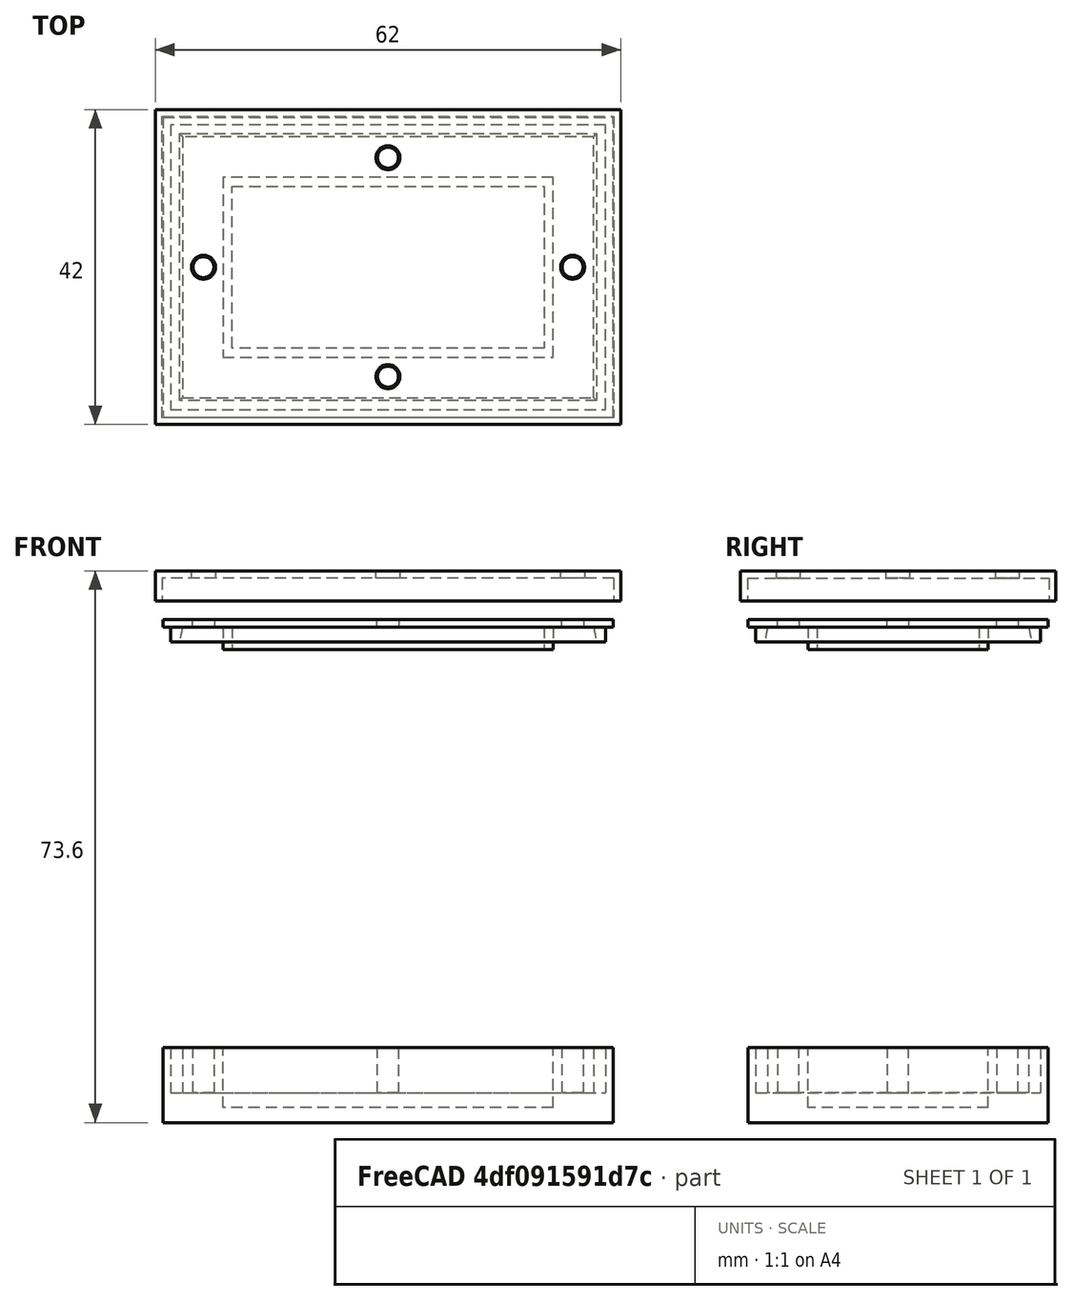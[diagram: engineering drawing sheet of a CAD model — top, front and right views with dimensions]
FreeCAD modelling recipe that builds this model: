
FCSTD DOCUMENT  (FreeCAD 1.0R39109 (Git))
Label: SealTest2
License: All rights reserved
objects: Sketcher::SketchObject×9, PartDesign::Pad×6, PartDesign::SubShapeBinder×4, PartDesign::Body×3, PartDesign::Pocket×1, PartDesign::AdditiveLoft×1
note: 49 computed .brp shape members not serialized (recipe doc carries the construction recipe); baked Part::Feature solids carry a one-line shape summary decoded from their .brp

FEATURE [Sketcher::SketchObject] Sketch  label="BaseSketch"
  ArcFitTolerance = 1e-06
  AttachmentSupport = -> [XY_Plane]
  FullyConstrained = true
  MakeInternals = false
  MapMode = 5
  sketch-geometry (4):
    g0: LineSegment StartX=-30 StartY=20 StartZ=0 EndX=-30 EndY=-20 EndZ=0
    g1: LineSegment StartX=-30 StartY=-20 StartZ=0 EndX=30 EndY=-20 EndZ=0
    g2: LineSegment StartX=30 StartY=-20 StartZ=0 EndX=30 EndY=20 EndZ=0
    g3: LineSegment StartX=30 StartY=20 StartZ=0 EndX=-30 EndY=20 EndZ=0
  constraints (11):
    c: Coincident(g0,g1)
    c: Coincident(g1,g2)
    c: Coincident(g2,g3)
    c: Coincident(g3,g0)
    c: Vertical(g0)
    c: Vertical(g2)
    c: Horizontal(g1)
    c: Horizontal(g3)
    c: DistanceX(g3,g3) = 60  'length'
    c: DistanceY(g2,g2) = 40  'width'
    c: Symmetric(g0,g2,g-1)
FEATURE [PartDesign::Pad] Pad  label="Base"
  Direction = (0,0,1)
  Length = 2
  Length2 = 10
  Profile = -> Sketch
  ReferenceAxis = -> Sketch [N_Axis]
  Suppressed = false
  Type = 0
FEATURE [Sketcher::SketchObject] Sketch001  label="WallSketch"
  ArcFitTolerance = 1e-06
  AttachmentSupport = -> [XY_Plane]
  FullyConstrained = true
  MakeInternals = false
  MapMode = 5
  expr: Constraints[10] = Sketch.Constraints.length
  expr: Constraints[11] = Sketch.Constraints.width
  sketch-geometry (10):
    g0: LineSegment StartX=30 StartY=-20 StartZ=0 EndX=30 EndY=20 EndZ=0
    g1: LineSegment StartX=30 StartY=20 StartZ=0 EndX=-30 EndY=20 EndZ=0
    g2: LineSegment StartX=-30 StartY=20 StartZ=0 EndX=-30 EndY=-20 EndZ=0
    g3: LineSegment StartX=-30 StartY=-20 StartZ=0 EndX=30 EndY=-20 EndZ=0
    g4: GeomPoint [constr] X=0 Y=0 Z=0
    g5: LineSegment StartX=22 StartY=-12 StartZ=0 EndX=22 EndY=12 EndZ=0
    g6: LineSegment StartX=22 StartY=12 StartZ=0 EndX=-22 EndY=12 EndZ=0
    g7: LineSegment StartX=-22 StartY=12 StartZ=0 EndX=-22 EndY=-12 EndZ=0
    g8: LineSegment StartX=-22 StartY=-12 StartZ=0 EndX=22 EndY=-12 EndZ=0
    g9: GeomPoint [constr] X=0 Y=0 Z=0
  constraints (24):
    c: Coincident(g0,g1)
    c: Coincident(g1,g2)
    c: Coincident(g2,g3)
    c: Coincident(g3,g0)
    c: Vertical(g0)
    c: Vertical(g2)
    c: Horizontal(g1)
    c: Horizontal(g3)
    c: Symmetric(g2,g0,g4)
    c: Coincident(g4,g-1)
    c: DistanceX(g1,g1) = 60
    c: DistanceY(g0,g0) = 40
    c: Coincident(g5,g6)
    c: Coincident(g6,g7)
    c: Coincident(g7,g8)
    c: Coincident(g8,g5)
    c: Vertical(g5)
    c: Vertical(g7)
    c: Horizontal(g6)
    c: Horizontal(g8)
    c: Symmetric(g7,g5,g9)
    c: Coincident(g9,g4)
    c: DistanceX(g1,g6) = 8
    c: DistanceY(g6,g1) = 8  'WallThickness'
FEATURE [PartDesign::Pad] Pad001  label="Wall"
  BaseFeature = -> Pad
  Direction = (0,0,1)
  Length = 10
  Length2 = 10
  Profile = -> Sketch001
  ReferenceAxis = -> Sketch001 [N_Axis]
  Suppressed = false
  Type = 0
FEATURE [Sketcher::SketchObject] Sketch002  label="SealGapSketch"
  ArcFitTolerance = 1e-06
  AttachmentSupport = -> [Pad001]
  ExternalGeometry = -> [Pad001]
  FullyConstrained = true
  MakeInternals = false
  MapMode = 5
  Placement = pos=(0,0,10) rot=(0,0,1;0rad)
  expr: Constraints[28] = <<WallSketch>>.Constraints.WallThickness - (.Constraints.SealFromSide + .Constraints.SealWidth)
  expr: Constraints[29] = <<WallSketch>>.Constraints.WallThickness - (.Constraints.SealFromSide + .Constraints.SealWidth)
  expr: Constraints[30] = <<WallSketch>>.Constraints.WallThickness - (.Constraints.SealFromSide + .Constraints.SealWidth)
  expr: Constraints[31] = <<WallSketch>>.Constraints.WallThickness - (.Constraints.SealFromSide + .Constraints.SealWidth)
  sketch-geometry (22):
    g0: LineSegment StartX=-27.4 StartY=17.4 StartZ=0 EndX=-27.4 EndY=-17.4 EndZ=0
    g1: LineSegment StartX=-27.4 StartY=-17.4 StartZ=0 EndX=27.4 EndY=-17.4 EndZ=0
    g2: LineSegment StartX=27.4 StartY=-17.4 StartZ=0 EndX=27.4 EndY=17.4 EndZ=0
    g3: LineSegment StartX=27.4 StartY=17.4 StartZ=0 EndX=-27.4 EndY=17.4 EndZ=0
    g4: GeomPoint [constr] X=0 Y=0 Z=0
    g5: LineSegment StartX=-29 StartY=-19 StartZ=0 EndX=29 EndY=-19 EndZ=0
    g6: LineSegment StartX=29 StartY=-19 StartZ=0 EndX=29 EndY=19 EndZ=0
    g7: LineSegment StartX=29 StartY=19 StartZ=0 EndX=-29 EndY=19 EndZ=0
    g8: LineSegment StartX=-29 StartY=19 StartZ=0 EndX=-29 EndY=-19 EndZ=0
    g9: GeomPoint [constr] X=0 Y=0 Z=0
    g10: Circle CenterX=0 CenterY=14.6 CenterZ=0 NormalX=0 NormalY=0 NormalZ=1 AngleXU=0 Radius=1.4
    g11: Circle CenterX=24.6 CenterY=0 CenterZ=0 NormalX=0 NormalY=0 NormalZ=1 AngleXU=0 Radius=1.4
    g12: Circle CenterX=0 CenterY=-14.6 CenterZ=0 NormalX=0 NormalY=0 NormalZ=1 AngleXU=0 Radius=1.4
    g13: Circle CenterX=-24.6 CenterY=0 CenterZ=0 NormalX=0 NormalY=0 NormalZ=1 AngleXU=0 Radius=1.4
    g14: LineSegment [constr] StartX=-30 StartY=20 StartZ=0 EndX=-30 EndY=19 EndZ=0
    g15: LineSegment [constr] StartX=-30 StartY=19 StartZ=0 EndX=-29 EndY=19 EndZ=0
    g16: LineSegment [constr] StartX=-29 StartY=19 StartZ=0 EndX=-29 EndY=20 EndZ=0
    g17: LineSegment [constr] StartX=-29 StartY=20 StartZ=0 EndX=-30 EndY=20 EndZ=0
    g18: LineSegment [constr] StartX=-29 StartY=19 StartZ=0 EndX=-29 EndY=17.4 EndZ=0
    g19: LineSegment [constr] StartX=-29 StartY=17.4 StartZ=0 EndX=-27.4 EndY=17.4 EndZ=0
    g20: LineSegment [constr] StartX=-27.4 StartY=17.4 StartZ=0 EndX=-27.4 EndY=19 EndZ=0
    g21: LineSegment [constr] StartX=-27.4 StartY=19 StartZ=0 EndX=-29 EndY=19 EndZ=0
  constraints (56):
    c: Coincident(g0,g1)
    c: Coincident(g1,g2)
    c: Coincident(g2,g3)
    c: Coincident(g3,g0)
    c: Vertical(g0)
    c: Vertical(g2)
    c: Horizontal(g1)
    c: Horizontal(g3)
    c: Symmetric(g2,g0,g4)
    c: Coincident(g4,g-1)
    c: Coincident(g5,g6)
    c: Coincident(g6,g7)
    c: Coincident(g7,g8)
    c: Coincident(g8,g5)
    c: Horizontal(g5)
    c: Horizontal(g7)
    c: Vertical(g6)
    c: Vertical(g8)
    c: Symmetric(g7,g5,g9)
    c: Coincident(g9,g4)
    c: PointOnObject(g10,g-2)
    c: PointOnObject(g11,g-1)
    c: PointOnObject(g12,g-2)
    c: PointOnObject(g13,g-1)
    c: Equal(g13,g10)
    c: Equal(g10,g11)
    c: Equal(g11,g12)
    c: Diameter(g10) = 2.8
    c: DistanceY(g10,g-3) = 5.4
    c: DistanceX(g-3,g13) = 5.4
    c: DistanceX(g11,g-3) = 5.4
    c: DistanceY(g-4,g12) = 5.4
    c: Coincident(g14,g15)
    c: Coincident(g15,g16)
    c: Coincident(g16,g17)
    c: Coincident(g17,g14)
    c: Vertical(g14)
    c: Vertical(g16)
    c: Horizontal(g15)
    c: Horizontal(g17)
    c: Coincident(g14,g-3)
    c: Coincident(g15,g7)
    c: Equal(g16,g15)
    c: Coincident(g18,g19)
    c: Coincident(g19,g20)
    c: Coincident(g20,g21)
    c: Coincident(g21,g18)
    c: Vertical(g18)
    c: Vertical(g20)
    c: Horizontal(g19)
    c: Horizontal(g21)
    c: Coincident(g18,g7)
    c: Coincident(g19,g0)
    c: Equal(g20,g19)
    c: DistanceX(g14,g16) = 1  'SealFromSide'
    c: DistanceX(g7,g20) = 1.6  'SealWidth'
FEATURE [PartDesign::Pocket] Pocket  label="SealGap"
  BaseFeature = -> Pad001
  Direction = (0,0,-1)
  Length = 6
  Length2 = 5
  Profile = -> Sketch002
  ReferenceAxis = -> Sketch002 [N_Axis]
  Suppressed = false
  Type = 0
FEATURE [PartDesign::Body] Body  label="Base001"
  AllowCompound = false
  Group = -> [Sketch,Pad,Sketch001,Pad001,Sketch002,Pocket]
  Origin = -> Origin
  Tip = -> Pocket
FEATURE [PartDesign::SubShapeBinder] Binder  label="SealGapsBinder"
  BindCopyOnChange = 0
  BindMode = 0
  ClaimChildren = false
  Context = -> Body001 [Binder.]
  Fuse = false
  MakeFace = true
  OffsetFill = false
  OffsetIntersection = false
  OffsetJoinType = 0
  OffsetOpenResult = false
  PartialLoad = false
  Relative = true
  Support = -> [Body[Sketch002.]]
  _Version = 2
FEATURE [PartDesign::SubShapeBinder] Binder001  label="BaseBinder"
  BindCopyOnChange = 0
  BindMode = 0
  ClaimChildren = false
  Context = -> Body001 [Binder001.]
  Fuse = false
  MakeFace = true
  OffsetFill = false
  OffsetIntersection = false
  OffsetJoinType = 0
  OffsetOpenResult = false
  PartialLoad = false
  Relative = true
  Support = -> [Body[Sketch.]]
  _Version = 2
FEATURE [Sketcher::SketchObject] Sketch003  label="SealBaseSketch"
  ArcFitTolerance = 1e-06
  AttachmentSupport = -> [XY_Plane001]
  ExternalGeometry = -> [Binder,Binder001]
  FullyConstrained = true
  MakeInternals = false
  MapMode = 5
  sketch-geometry (10):
    g0: LineSegment StartX=30 StartY=20 StartZ=0 EndX=30 EndY=-20 EndZ=0
    g1: LineSegment StartX=-30 StartY=-20 StartZ=0 EndX=-30 EndY=20 EndZ=0
    g2: LineSegment StartX=-30 StartY=20 StartZ=0 EndX=30 EndY=20 EndZ=0
    g3: GeomPoint [constr] X=0 Y=0 Z=0
    g4: GeomPoint [constr] X=0 Y=0 Z=0
    g5: LineSegment StartX=-30 StartY=-20 StartZ=0 EndX=30 EndY=-20 EndZ=0
    g6: Circle CenterX=0 CenterY=14.6 CenterZ=0 NormalX=0 NormalY=0 NormalZ=1 AngleXU=0 Radius=1.45
    g7: Circle CenterX=24.6 CenterY=0 CenterZ=0 NormalX=0 NormalY=0 NormalZ=1 AngleXU=0 Radius=1.45
    g8: Circle CenterX=0 CenterY=-14.6 CenterZ=0 NormalX=0 NormalY=0 NormalZ=1 AngleXU=0 Radius=1.45
    g9: Circle CenterX=-24.6 CenterY=0 CenterZ=0 NormalX=0 NormalY=0 NormalZ=1 AngleXU=0 Radius=1.45
  constraints (20):
    c: Coincident(g1,g2)
    c: Coincident(g2,g0)
    c: Vertical(g0)
    c: Vertical(g1)
    c: Horizontal(g2)
    c: Symmetric(g1,g0,g3)
    c: Coincident(g3,g-1)
    c: Coincident(g4,g3)
    c: Coincident(g5,g1)
    c: Coincident(g5,g0)
    c: Horizontal(g5)
    c: Coincident(g0,g-7)
    c: Coincident(g6,g-4)
    c: Coincident(g7,g-5)
    c: Coincident(g8,g-6)
    c: Coincident(g9,g-3)
    c: Equal(g9,g8)
    c: Equal(g8,g7)
    c: Equal(g7,g6)
    c: Diameter(g6) = 2.9
FEATURE [PartDesign::Pad] Pad002  label="SealBase"
  Direction = (0,0,1)
  Length = 1
  Length2 = 10
  Profile = -> Sketch003
  ReferenceAxis = -> Sketch003 [N_Axis]
  Suppressed = false
  Type = 0
FEATURE [Sketcher::SketchObject] Sketch004  label="SealGapBaseSketch"
  ArcFitTolerance = 1e-06
  AttachmentOffset = pos=(0,0,1) rot=(0,0,1;0rad)
  AttachmentSupport = -> [XY_Plane001]
  ExternalGeometry = -> [Binder]
  FullyConstrained = true
  MakeInternals = false
  MapMode = 5
  Placement = pos=(0,0,1) rot=(0,0,1;0rad)
  expr: Constraints[32] = <<SealGapSketch>>.Constraints.SealWidth
  sketch-geometry (14):
    g0: LineSegment StartX=29 StartY=19 StartZ=0 EndX=29 EndY=-19 EndZ=0
    g1: LineSegment StartX=29 StartY=-19 StartZ=0 EndX=-29 EndY=-19 EndZ=0
    g2: LineSegment StartX=-29 StartY=-19 StartZ=0 EndX=-29 EndY=19 EndZ=0
    g3: LineSegment StartX=-29 StartY=19 StartZ=0 EndX=29 EndY=19 EndZ=0
    g4: GeomPoint [constr] X=0 Y=0 Z=0
    g5: LineSegment StartX=-27.4 StartY=-17.4 StartZ=0 EndX=-27.4 EndY=17.4 EndZ=0
    g6: LineSegment StartX=-27.4 StartY=17.4 StartZ=0 EndX=27.4 EndY=17.4 EndZ=0
    g7: LineSegment StartX=27.4 StartY=17.4 StartZ=0 EndX=27.4 EndY=-17.4 EndZ=0
    g8: LineSegment StartX=27.4 StartY=-17.4 StartZ=0 EndX=-27.4 EndY=-17.4 EndZ=0
    g9: GeomPoint [constr] X=0 Y=0 Z=0
    g10: LineSegment [constr] StartX=-29 StartY=19 StartZ=0 EndX=-29 EndY=17.4 EndZ=0
    g11: LineSegment [constr] StartX=-29 StartY=17.4 StartZ=0 EndX=-27.4 EndY=17.4 EndZ=0
    g12: LineSegment [constr] StartX=-27.4 StartY=17.4 StartZ=0 EndX=-27.4 EndY=19 EndZ=0
    g13: LineSegment [constr] StartX=-27.4 StartY=19 StartZ=0 EndX=-29 EndY=19 EndZ=0
  constraints (33):
    c: Coincident(g0,g1)
    c: Coincident(g1,g2)
    c: Coincident(g2,g3)
    c: Coincident(g3,g0)
    c: Vertical(g0)
    c: Vertical(g2)
    c: Horizontal(g1)
    c: Horizontal(g3)
    c: Symmetric(g2,g0,g4)
    c: Coincident(g4,g-1)
    c: Coincident(g1,g-3)
    c: Coincident(g5,g6)
    c: Coincident(g6,g7)
    c: Coincident(g7,g8)
    c: Coincident(g8,g5)
    c: Vertical(g5)
    c: Vertical(g7)
    c: Horizontal(g6)
    c: Horizontal(g8)
    c: Symmetric(g7,g5,g9)
    c: Coincident(g9,g4)
    c: Coincident(g10,g11)
    c: Coincident(g11,g12)
    c: Coincident(g12,g13)
    c: Coincident(g13,g10)
    c: Vertical(g10)
    c: Vertical(g12)
    c: Horizontal(g11)
    c: Horizontal(g13)
    c: Coincident(g10,g2)
    c: Coincident(g5,g11)
    c: Equal(g12,g11)
    c: DistanceY(g10,g2) = 1.6
FEATURE [PartDesign::SubShapeBinder] Binder002  label="WallSketchBinder"
  BindCopyOnChange = 0
  BindMode = 0
  ClaimChildren = false
  Context = -> Body001 [Binder002.]
  Fuse = false
  MakeFace = true
  OffsetFill = false
  OffsetIntersection = false
  OffsetJoinType = 0
  OffsetOpenResult = false
  PartialLoad = false
  Relative = true
  Support = -> [Body[Sketch001.]]
  _Version = 2
FEATURE [Sketcher::SketchObject] Sketch005  label="SealGapRaisedSketch"
  ArcFitTolerance = 1e-06
  AttachmentOffset = pos=(0,0,3) rot=(0,0,1;0rad)
  AttachmentSupport = -> [XY_Plane001]
  ExternalGeometry = -> [Binder]
  FullyConstrained = true
  MakeInternals = false
  MapMode = 5
  Placement = pos=(0,0,3) rot=(0,0,1;0rad)
  expr: Constraints[32] = 1.2 mm
  sketch-geometry (14):
    g0: LineSegment StartX=-29 StartY=-19 StartZ=0 EndX=29 EndY=-19 EndZ=0
    g1: LineSegment StartX=29 StartY=-19 StartZ=0 EndX=29 EndY=19 EndZ=0
    g2: LineSegment StartX=29 StartY=19 StartZ=0 EndX=-29 EndY=19 EndZ=0
    g3: LineSegment StartX=-29 StartY=19 StartZ=0 EndX=-29 EndY=-19 EndZ=0
    g4: GeomPoint [constr] X=0 Y=0 Z=0
    g5: LineSegment StartX=27.8 StartY=-17.8 StartZ=0 EndX=27.8 EndY=17.8 EndZ=0
    g6: LineSegment StartX=27.8 StartY=17.8 StartZ=0 EndX=-27.8 EndY=17.8 EndZ=0
    g7: LineSegment StartX=-27.8 StartY=17.8 StartZ=0 EndX=-27.8 EndY=-17.8 EndZ=0
    g8: LineSegment StartX=-27.8 StartY=-17.8 StartZ=0 EndX=27.8 EndY=-17.8 EndZ=0
    g9: GeomPoint [constr] X=0 Y=0 Z=0
    g10: LineSegment [constr] StartX=-29 StartY=19 StartZ=0 EndX=-29 EndY=17.8 EndZ=0
    g11: LineSegment [constr] StartX=-29 StartY=17.8 StartZ=0 EndX=-27.8 EndY=17.8 EndZ=0
    g12: LineSegment [constr] StartX=-27.8 StartY=17.8 StartZ=0 EndX=-27.8 EndY=19 EndZ=0
    g13: LineSegment [constr] StartX=-27.8 StartY=19 StartZ=0 EndX=-29 EndY=19 EndZ=0
  constraints (33):
    c: Coincident(g0,g1)
    c: Coincident(g1,g2)
    c: Coincident(g2,g3)
    c: Coincident(g3,g0)
    c: Horizontal(g0)
    c: Horizontal(g2)
    c: Vertical(g1)
    c: Vertical(g3)
    c: Symmetric(g2,g0,g4)
    c: Coincident(g4,g-1)
    c: Coincident(g1,g-3)
    c: Coincident(g5,g6)
    c: Coincident(g6,g7)
    c: Coincident(g7,g8)
    c: Coincident(g8,g5)
    c: Vertical(g5)
    c: Vertical(g7)
    c: Horizontal(g6)
    c: Horizontal(g8)
    c: Symmetric(g7,g5,g9)
    c: Coincident(g9,g4)
    c: Coincident(g10,g11)
    c: Coincident(g11,g12)
    c: Coincident(g12,g13)
    c: Coincident(g13,g10)
    c: Vertical(g10)
    c: Vertical(g12)
    c: Horizontal(g11)
    c: Horizontal(g13)
    c: Coincident(g10,g2)
    c: Coincident(g11,g6)
    c: Equal(g12,g11)
    c: DistanceY(g10,g2) = 1.2
FEATURE [PartDesign::AdditiveLoft] AdditiveLoft
  BaseFeature = -> Pad002
  Closed = false
  Profile = -> Sketch004
  Ruled = false
  Sections = -> [Sketch005]
  Suppressed = false
FEATURE [Sketcher::SketchObject] Sketch008
  ArcFitTolerance = 1e-06
  AttachmentSupport = -> [XY_Plane002]
  FullyConstrained = true
  MakeInternals = false
  MapMode = 5
  expr: Constraints[20] = <<LidBaseSketch>>.Constraints.LidLength
  expr: Constraints[21] = <<LidBaseSketch>>.Constraints.LidWidth
  sketch-geometry (14):
    g0: LineSegment StartX=31 StartY=-21 StartZ=0 EndX=31 EndY=21 EndZ=0
    g1: LineSegment StartX=31 StartY=21 StartZ=0 EndX=-31 EndY=21 EndZ=0
    g2: LineSegment StartX=-31 StartY=21 StartZ=0 EndX=-31 EndY=-21 EndZ=0
    g3: LineSegment StartX=-31 StartY=-21 StartZ=0 EndX=31 EndY=-21 EndZ=0
    g4: GeomPoint [constr] X=0 Y=0 Z=0
    g5: LineSegment StartX=-30.1 StartY=-20.1 StartZ=0 EndX=30.1 EndY=-20.1 EndZ=0
    g6: LineSegment StartX=30.1 StartY=-20.1 StartZ=0 EndX=30.1 EndY=20.1 EndZ=0
    g7: LineSegment StartX=30.1 StartY=20.1 StartZ=0 EndX=-30.1 EndY=20.1 EndZ=0
    g8: LineSegment StartX=-30.1 StartY=20.1 StartZ=0 EndX=-30.1 EndY=-20.1 EndZ=0
    g9: GeomPoint [constr] X=0 Y=0 Z=0
    g10: LineSegment [constr] StartX=-31 StartY=21 StartZ=0 EndX=-31 EndY=20.1 EndZ=0
    g11: LineSegment [constr] StartX=-31 StartY=20.1 StartZ=0 EndX=-30.1 EndY=20.1 EndZ=0
    g12: LineSegment [constr] StartX=-30.1 StartY=20.1 StartZ=0 EndX=-30.1 EndY=21 EndZ=0
    g13: LineSegment [constr] StartX=-30.1 StartY=21 StartZ=0 EndX=-31 EndY=21 EndZ=0
  constraints (34):
    c: Coincident(g0,g1)
    c: Coincident(g1,g2)
    c: Coincident(g2,g3)
    c: Coincident(g3,g0)
    c: Vertical(g0)
    c: Vertical(g2)
    c: Horizontal(g1)
    c: Horizontal(g3)
    c: Symmetric(g2,g0,g4)
    c: Coincident(g4,g-1)
    c: Coincident(g5,g6)
    c: Coincident(g6,g7)
    c: Coincident(g7,g8)
    c: Coincident(g8,g5)
    c: Horizontal(g5)
    c: Horizontal(g7)
    c: Vertical(g6)
    c: Vertical(g8)
    c: Symmetric(g7,g5,g9)
    c: Coincident(g9,g4)
    c: DistanceX(g1,g1) = 62
    c: DistanceY(g0,g0) = 42
    c: Coincident(g10,g11)
    c: Coincident(g11,g12)
    c: Coincident(g12,g13)
    c: Coincident(g13,g10)
    c: Vertical(g10)
    c: Vertical(g12)
    c: Horizontal(g11)
    c: Horizontal(g13)
    c: Coincident(g10,g1)
    c: Coincident(g11,g7)
    c: Equal(g12,g11)
    c: DistanceY(g10,g1) = 0.9
FEATURE [PartDesign::SubShapeBinder] Binder003  label="SealGapBinder"
  BindCopyOnChange = 0
  BindMode = 0
  ClaimChildren = false
  Context = -> Body002 [Binder003.]
  Fuse = false
  MakeFace = true
  OffsetFill = false
  OffsetIntersection = false
  OffsetJoinType = 0
  OffsetOpenResult = false
  PartialLoad = false
  Relative = true
  Support = -> [Body[Sketch002.]]
  _Version = 2
FEATURE [Sketcher::SketchObject] Sketch006  label="LidBaseSketch"
  ArcFitTolerance = 1e-06
  AttachmentSupport = -> [XY_Plane002]
  ExternalGeometry = -> [Binder003]
  FullyConstrained = true
  MakeInternals = false
  MapMode = 5
  expr: .Constraints.LidLength = <<BaseSketch>>.Constraints.length + 2 mm
  expr: .Constraints.LidWidth = <<BaseSketch>>.Constraints.width + 2 mm
  sketch-geometry (9):
    g0: LineSegment StartX=31 StartY=-21 StartZ=0 EndX=31 EndY=21 EndZ=0
    g1: LineSegment StartX=31 StartY=21 StartZ=0 EndX=-31 EndY=21 EndZ=0
    g2: LineSegment StartX=-31 StartY=21 StartZ=0 EndX=-31 EndY=-21 EndZ=0
    g3: LineSegment StartX=-31 StartY=-21 StartZ=0 EndX=31 EndY=-21 EndZ=0
    g4: GeomPoint [constr] X=0 Y=0 Z=0
    g5: Circle CenterX=0 CenterY=14.6 CenterZ=0 NormalX=0 NormalY=0 NormalZ=1 AngleXU=0 Radius=1.6
    g6: Circle CenterX=-24.6 CenterY=0 CenterZ=0 NormalX=0 NormalY=0 NormalZ=1 AngleXU=0 Radius=1.6
    g7: Circle CenterX=0 CenterY=-14.6 CenterZ=0 NormalX=0 NormalY=0 NormalZ=1 AngleXU=0 Radius=1.6
    g8: Circle CenterX=24.6 CenterY=0 CenterZ=0 NormalX=0 NormalY=0 NormalZ=1 AngleXU=0 Radius=1.6
  constraints (20):
    c: Coincident(g0,g1)
    c: Coincident(g1,g2)
    c: Coincident(g2,g3)
    c: Coincident(g3,g0)
    c: Vertical(g0)
    c: Vertical(g2)
    c: Horizontal(g1)
    c: Horizontal(g3)
    c: Symmetric(g2,g0,g4)
    c: Coincident(g4,g-1)
    c: DistanceX(g1,g1) = 62  'LidLength'
    c: DistanceY(g0,g0) = 42  'LidWidth'
    c: Coincident(g5,g-3)
    c: Coincident(g6,g-4)
    c: Coincident(g7,g-5)
    c: Coincident(g8,g-6)
    c: Equal(g8,g5)
    c: Equal(g5,g6)
    c: Equal(g6,g7)
    c: Diameter(g5) = 3.2
FEATURE [PartDesign::Pad] Pad003  label="LidBase"
  Direction = (0,0,1)
  Length = 1
  Length2 = 10
  Profile = -> Sketch006
  ReferenceAxis = -> Sketch006 [N_Axis]
  Suppressed = false
  Type = 0
FEATURE [PartDesign::Pad] Pad004  label="LidWall"
  BaseFeature = -> Pad003
  Direction = (0,0,1)
  Length = 4
  Length2 = 10
  Profile = -> Sketch008
  ReferenceAxis = -> Sketch008 [N_Axis]
  Suppressed = false
  Type = 0
FEATURE [PartDesign::Body] Body002  label="Lid"
  AllowCompound = false
  Group = -> [Sketch006,Pad003,Sketch008,Pad004,Binder003]
  Origin = -> Origin002
  Placement = pos=(0,3.8e-15,73.6) rot=(1,0,0;3.14159rad)
  Tip = -> Pad004
FEATURE [Sketcher::SketchObject] Sketch009
  ArcFitTolerance = 1e-06
  AttachmentSupport = -> [XY_Plane001]
  FullyConstrained = true
  MakeInternals = false
  MapMode = 5
  expr: Constraints[40] = <<BaseSketch>>.Constraints.width
  expr: Constraints[41] = <<BaseSketch>>.Constraints.length
  expr: Constraints[42] = <<WallSketch>>.Constraints.WallThickness
  expr: Constraints[43] = <<WallSketch>>.Constraints.WallThickness
  sketch-geometry (17):
    g0: LineSegment StartX=-22 StartY=12 StartZ=0 EndX=-22 EndY=-12 EndZ=0
    g1: LineSegment StartX=-22 StartY=-12 StartZ=0 EndX=22 EndY=-12 EndZ=0
    g2: LineSegment StartX=22 StartY=-12 StartZ=0 EndX=22 EndY=12 EndZ=0
    g3: LineSegment StartX=22 StartY=12 StartZ=0 EndX=-22 EndY=12 EndZ=0
    g4: LineSegment StartX=-20.8 StartY=10.8 StartZ=0 EndX=-20.8 EndY=-10.8 EndZ=0
    g5: LineSegment StartX=-20.8 StartY=-10.8 StartZ=0 EndX=20.8 EndY=-10.8 EndZ=0
    g6: LineSegment StartX=20.8 StartY=-10.8 StartZ=0 EndX=20.8 EndY=10.8 EndZ=0
    g7: LineSegment StartX=20.8 StartY=10.8 StartZ=0 EndX=-20.8 EndY=10.8 EndZ=0
    g8: LineSegment [constr] StartX=22 StartY=12 StartZ=0 EndX=20.8 EndY=12 EndZ=0
    g9: LineSegment [constr] StartX=20.8 StartY=12 StartZ=0 EndX=20.8 EndY=10.8 EndZ=0
    g10: LineSegment [constr] StartX=20.8 StartY=10.8 StartZ=0 EndX=22 EndY=10.8 EndZ=0
    g11: LineSegment [constr] StartX=22 StartY=10.8 StartZ=0 EndX=22 EndY=12 EndZ=0
    g12: LineSegment [constr] StartX=30 StartY=-20 StartZ=0 EndX=30 EndY=20 EndZ=0
    g13: LineSegment [constr] StartX=30 StartY=20 StartZ=0 EndX=-30 EndY=20 EndZ=0
    g14: LineSegment [constr] StartX=-30 StartY=20 StartZ=0 EndX=-30 EndY=-20 EndZ=0
    g15: LineSegment [constr] StartX=-30 StartY=-20 StartZ=0 EndX=30 EndY=-20 EndZ=0
    g16: GeomPoint [constr] X=0 Y=0 Z=0
  constraints (44):
    c: Coincident(g0,g1)
    c: Coincident(g1,g2)
    c: Coincident(g2,g3)
    c: Coincident(g3,g0)
    c: Vertical(g0)
    c: Vertical(g2)
    c: Horizontal(g1)
    c: Horizontal(g3)
    c: Coincident(g4,g5)
    c: Coincident(g5,g6)
    c: Coincident(g6,g7)
    c: Coincident(g7,g4)
    c: Vertical(g4)
    c: Vertical(g6)
    c: Horizontal(g5)
    c: Horizontal(g7)
    c: Symmetric(g4,g6,g-1)
    c: Symmetric(g2,g0,g-1)
    c: Coincident(g8,g9)
    c: Coincident(g9,g10)
    c: Coincident(g10,g11)
    c: Coincident(g11,g8)
    c: Horizontal(g8)
    c: Horizontal(g10)
    c: Vertical(g9)
    c: Vertical(g11)
    c: Coincident(g8,g2)
    c: Coincident(g9,g6)
    c: Equal(g9,g10)
    c: DistanceY(g10,g2) = 1.2
    c: Coincident(g12,g13)
    c: Coincident(g13,g14)
    c: Coincident(g14,g15)
    c: Coincident(g15,g12)
    c: Vertical(g12)
    c: Vertical(g14)
    c: Horizontal(g13)
    c: Horizontal(g15)
    c: Symmetric(g14,g12,g16)
    c: Coincident(g16,g-1)
    c: DistanceY(g12,g12) = 40
    c: DistanceX(g13,g13) = 60
    c: DistanceY(g0,g13) = 8
    c: DistanceX(g13,g0) = 8
FEATURE [PartDesign::Pad] Pad005
  BaseFeature = -> AdditiveLoft
  Direction = (0,0,1)
  Length = 4
  Length2 = 10
  Profile = -> Sketch009
  ReferenceAxis = -> Sketch009 [N_Axis]
  Suppressed = false
  Type = 0
FEATURE [PartDesign::Body] Body001  label="Seal"
  AllowCompound = false
  Group = -> [Binder,Sketch003,Binder001,Pad002,Sketch004,Binder002,Sketch005,AdditiveLoft,Sketch009,Pad005]
  Origin = -> Origin001
  Placement = pos=(0,6.6e-15,67.1) rot=(1,0,0;3.14159rad)
  Tip = -> Pad005
